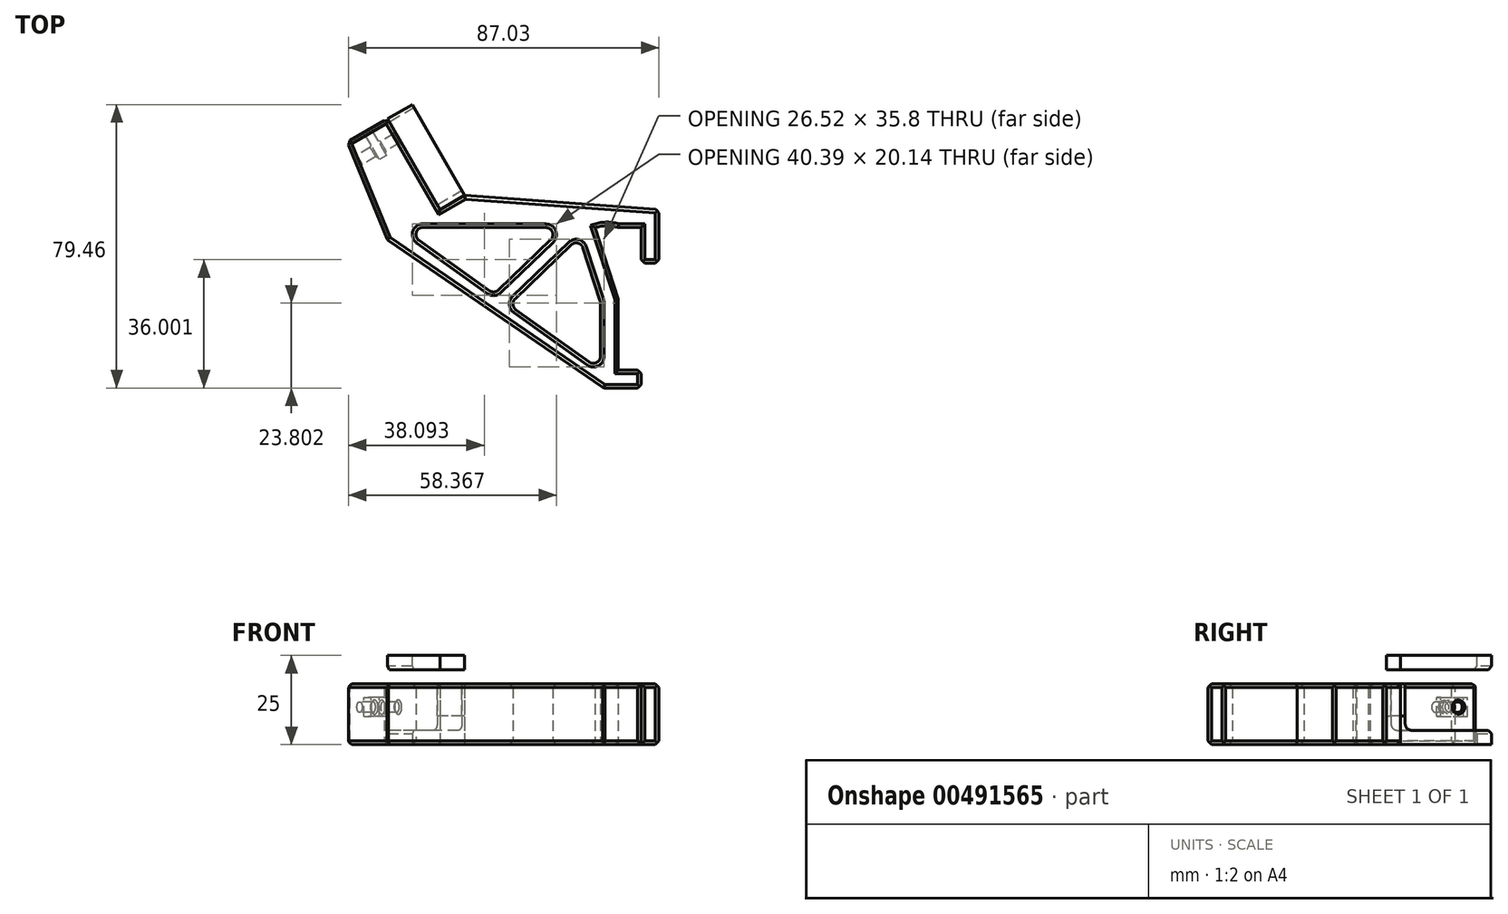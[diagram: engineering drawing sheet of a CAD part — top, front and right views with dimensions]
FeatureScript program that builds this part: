
annotation { "Feature Type Name" : "Feature", "Feature Type Description" : "" }
export const myFeature = defineFeature(function(context is Context, id is Id, definition is map)
    precondition{}
    {
        {
            assignVariable(context, id + "F0", {"name" : "nutDepth", "anyValue" : 2.32});
        }
        {
            assignVariable(context, id + "F1", {"name" : "rightSide", "anyValue" : 1});
        }
        {
            var Q0;
            Q0=qCreatedBy(makeId("Top.planeOp"),FACE);
            var sketch = newSketch(context, id + "F2", { "sketchPlane" : qUnion([Q0])});
            skLineSegment(sketch, "E0", {"start": v(0, 0) * mm, "end": v(0, 20) * mm});
            skLineSegment(sketch, "E1", {"start": v(0, 0) * mm, "end": v(6.4, 0) * mm});
            skLineSegment(sketch, "E2", {"start": v(6.4, 0) * mm, "end": v(6.4, -5) * mm});
            skLineSegment(sketch, "E3", {"start": v(6.4, -5) * mm, "end": v(-5, -5) * mm});
            skLineSegment(sketch, "E4", {"start": v(0, 40) * mm, "end": v(6.4, 40) * mm});
            skLineSegment(sketch, "E5", {"start": v(6.4, 40) * mm, "end": v(6.4, 30) * mm});
            skLineSegment(sketch, "E6", {"start": v(6.4, 30) * mm, "end": v(11.4, 30) * mm});
            skLineSegment(sketch, "E7", {"start": v(11.4, 30) * mm, "end": v(11.4, 45) * mm});
            skLineSegment(sketch, "E8", {"start": v(0, 20) * mm, "end": v(-6.5, 40) * mm});
            skArc(sketch, "E9", {"start": v(0, 40) * mm, "mid": v(-3.25, 40.51) * mm, "end": v(-6.5, 40) * mm});
            skLineSegment(sketch, "E10", {"start": v(11.4, 45) * mm, "end": v(0, 45) * mm, "construction": true});
            skLineSegment(sketch, "E11", {"start": v(0, 45) * mm, "end": v(-50, 45) * mm, "construction": true});
            skLineSegment(sketch, "E12", {"start": v(-50, 45) * mm, "end": v(11.4, 45) * mm, "construction": true});
            skLineSegment(sketch, "E13", {"start": v(-50, 45) * mm, "end": v(-64.7, 70.46) * mm});
            skLineSegment(sketch, "E14", {"start": v(-50, 45) * mm, "end": v(-43.07, 49) * mm});
            skLineSegment(sketch, "E15", {"start": v(-64.7, 70.46) * mm, "end": v(-75.96, 63.96) * mm});
            skLineSegment(sketch, "E16", {"start": v(-50, 45) * mm, "end": v(-54.33, 42.5) * mm, "construction": true});
            skLineSegment(sketch, "E17", {"start": v(-64.7, 70.46) * mm, "end": v(-61.7, 65.26) * mm, "construction": true});
            skLineSegment(sketch, "E18.0", {"start": v(-5, 3.9) * mm, "end": v(-5, 18.9) * mm});
            skLineSegment(sketch, "E19.0", {"start": v(-5.1, 19.5) * mm, "end": v(-9.91, 34.32) * mm});
            skLineSegment(sketch, "E20", {"start": v(-40.93, 40) * mm, "end": v(-20.33, 40) * mm});
            skLineSegment(sketch, "E21", {"start": v(-43.07, 49) * mm, "end": v(11.4, 45) * mm});
            skPoint(sketch, "E22.0.midPoint", {"position": v(-5.37, 18.33) * mm});
            skLineSegment(sketch, "E23", {"start": v(-75.96, 63.96) * mm, "end": v(-64.7, 36.54) * mm});
            skPoint(sketch, "E24.visualSharp", {"position": v(-61.03, 40.13) * mm});
            skPoint(sketch, "E25.newPointB", {"position": v(15.42, -35.63) * mm});
            skPoint(sketch, "E26.visualSharp", {"position": v(-45.4, 40) * mm});
            skArc(sketch, "E27.filletArc", {"start": v(-5, 18.9) * mm, "mid": v(-5.02, 19.2) * mm, "end": v(-5.1, 19.5) * mm});
            skLineSegment(sketch, "E28", {"start": v(-5, -5) * mm, "end": v(-5, 0) * mm, "construction": true});
            skLineSegment(sketch, "E29", {"start": v(-64.7, 36.54) * mm, "end": v(-4.1, -5) * mm});
            skLineSegment(sketch, "E30", {"start": v(-55.9, 36.44) * mm, "end": v(-36.14, 22.3) * mm});
            skLineSegment(sketch, "E31", {"start": v(-40.93, 40) * mm, "end": v(-52.7, 40.06) * mm});
            skPoint(sketch, "E32.trimOffspring.end.orphan", {"position": v(-66.18, 40.13) * mm});
            skPoint(sketch, "E33.visualSharp", {"position": v(-5, 0) * mm});
            skArc(sketch, "E33.filletArc", {"start": v(-8.16, 2.27) * mm, "mid": v(-6.09, 2.11) * mm, "end": v(-5, 3.9) * mm});
            skLineSegment(sketch, "E34.0", {"start": v(-13.2, 35.15) * mm, "end": v(-28.92, 20.04) * mm});
            skLineSegment(sketch, "E35", {"start": v(-18.94, 36.56) * mm, "end": v(-33.59, 22.48) * mm});
            skLineSegment(sketch, "E36.trimOffspring", {"start": v(-28.7, 16.97) * mm, "end": v(-8.16, 2.27) * mm});
            skArc(sketch, "E37.filletArc", {"start": v(-9.91, 34.32) * mm, "mid": v(-11.33, 35.64) * mm, "end": v(-13.2, 35.15) * mm});
            skPoint(sketch, "E38.visualSharp", {"position": v(-30.65, 18.37) * mm});
            skArc(sketch, "E38.filletArc", {"start": v(-28.92, 20.04) * mm, "mid": v(-29.53, 18.45) * mm, "end": v(-28.7, 16.97) * mm});
            skArc(sketch, "E39.filletArc", {"start": v(-18.94, 36.56) * mm, "mid": v(-18.48, 38.75) * mm, "end": v(-20.33, 40) * mm});
            skPoint(sketch, "E40.visualSharp", {"position": v(-34.79, 21.33) * mm});
            skArc(sketch, "E40.filletArc", {"start": v(-36.14, 22.3) * mm, "mid": v(-34.83, 21.93) * mm, "end": v(-33.59, 22.48) * mm});
            skLineSegment(sketch, "E41", {"start": v(-52.7, 40.06) * mm, "end": v(-54.72, 40.07) * mm});
            skArc(sketch, "E42.filletArc", {"start": v(-54.72, 40.07) * mm, "mid": v(-56.64, 38.69) * mm, "end": v(-55.9, 36.44) * mm});
            skLineSegment(sketch, "E43", {"start": v(0, 20) * mm, "end": v(0, 40) * mm, "construction": true});
            skSolve(sketch);
        }
        {
            var Q0;
            Q0=makeQuery(id+"F2.imprint","IMPRINT",FACE,{"disambiguationData":[TD([[makeQuery(id+"F2.imprint","IMPRINT",EDGE,{"derivedFrom":sQuery(id+"F2.wireOp",EDGE,"E0")}),1.0]])]});
            var Q1;
            Q1=makeQuery(id+"F2.imprint","IMPRINT",FACE,{"disambiguationData":[TD([[makeQuery(id+"F2.imprint","IMPRINT",EDGE,{"derivedFrom":sQuery(id+"F2.wireOp",EDGE,"237edecc-037b-4469-a4d6-ffe34dbb8c16.0")}),-1.0]])]});
            var Q2;
            Q2=makeQuery(id+"F2.imprint","IMPRINT",FACE,{"disambiguationData":[TD([[makeQuery(id+"F2.imprint","IMPRINT",EDGE,{"derivedFrom":sQuery(id+"F2.wireOp",EDGE,"E12")}),1.0]])]});
            var Q3;
            {var subQ1=sQuery(id+"F2.wireOp",EDGE,"eAJWAXpk-Rpyz-sTjt-Ieoh-9hGECF5WtqjO");Q3=makeQuery(id+"F2.imprint","IMPRINT",FACE,{"disambiguationData":[TD([[makeQuery(id+"F2.imprint","IMPRINT",EDGE,{"derivedFrom":subQ1}),-1.0]])]});}
            var Q4;
            Q4=sQuery(id+"F2.wireOp",EDGE,"E16");
            extrude(context, id + "F3", {"entities" : qUnion([Q0, Q1, Q2, Q3]), "surfaceEntities" : qUnion([Q4]), "depth" : 17 * mm, "offsetDistance" : 25 * mm});
        }
        {
            var Q0;
            Q0=makeQuery(id+"F3.opExtrude","SWEPT_FACE",FACE,{"disambiguationData":[OSD([sQuery(id+"F2.wireOp",EDGE,"E13")])]});
            var sketch = newSketch(context, id + "F4", { "sketchPlane" : qUnion([Q0])});
            skPoint(sketch, "E44.0", {"position": v(87.37, 0) * mm});
            skLineSegment(sketch, "E45", {"start": v(87.37, 0) * mm, "end": v(87.37, 17) * mm, "construction": true});
            skCircle(sketch, "E46", {"center": v(87.37, 8.5) * mm, "radius": 1.5 * mm});
            skLineSegment(sketch, "E47", {"start": v(87.37, 8.5) * mm, "end": v(65.47, 8.5) * mm, "construction": true});
            skPoint(sketch, "E48.newPointB", {"position": v(63.97, 17) * mm});
            skPoint(sketch, "E49.newPointA", {"position": v(65.47, 0) * mm});
            skPoint(sketch, "E49.newPointB", {"position": v(63.97, 0) * mm});
            skPoint(sketch, "E50.0", {"position": v(93.37, 0) * mm});
            skLineSegment(sketch, "E51", {"start": v(54.97, 17) * mm, "end": v(93.37, 17) * mm});
            skLineSegment(sketch, "E52", {"start": v(54.97, 17) * mm, "end": v(54.97, 13) * mm, "construction": true});
            skLineSegment(sketch, "E53", {"start": v(67.47, 17) * mm, "end": v(54.97, 17) * mm});
            skPoint(sketch, "E54.orphan", {"position": v(54.97, 0) * mm});
            skLineSegment(sketch, "E55", {"start": v(63.97, 17) * mm, "end": v(63.97, 21) * mm});
            skLineSegment(sketch, "E56", {"start": v(93.37, 17) * mm, "end": v(93.37, 21) * mm});
            skLineSegment(sketch, "E57", {"start": v(93.37, 21) * mm, "end": v(63.97, 21) * mm});
            skLineSegment(sketch, "E58", {"start": v(63.97, 17) * mm, "end": v(63.97, 4) * mm});
            skLineSegment(sketch, "E59", {"start": v(63.97, 4) * mm, "end": v(65.47, 4) * mm});
            skLineSegment(sketch, "E60", {"start": v(65.47, 4) * mm, "end": v(65.47, 15) * mm});
            skLineSegment(sketch, "E61", {"start": v(67.47, 17) * mm, "end": v(93.37, 17) * mm});
            skPoint(sketch, "E62.visualSharp", {"position": v(65.47, 17) * mm});
            skArc(sketch, "E62.filletArc", {"start": v(67.47, 17) * mm, "mid": v(66.06, 16.41) * mm, "end": v(65.47, 15) * mm});
            skLineSegment(sketch, "E63", {"start": v(93.37, 0) * mm, "end": v(93.37, -4) * mm});
            skLineSegment(sketch, "E64", {"start": v(63.97, 0) * mm, "end": v(63.97, -4) * mm});
            skLineSegment(sketch, "E65", {"start": v(63.97, -4) * mm, "end": v(93.37, -4) * mm});
            skLineSegment(sketch, "E66", {"start": v(63.97, 0) * mm, "end": v(63.97, 13) * mm});
            skLineSegment(sketch, "E67", {"start": v(63.97, 13) * mm, "end": v(65.47, 13) * mm});
            skLineSegment(sketch, "E68", {"start": v(65.47, 13) * mm, "end": v(65.47, 2) * mm});
            skLineSegment(sketch, "E69", {"start": v(54.97, 0) * mm, "end": v(67.47, 0) * mm});
            skArc(sketch, "E70.filletArc", {"start": v(65.47, 2) * mm, "mid": v(66.06, 0.59) * mm, "end": v(67.47, 0) * mm});
            skLineSegment(sketch, "E71", {"start": v(54.97, 0) * mm, "end": v(93.37, 0) * mm});
            skSolve(sketch);
        }
        {
            var Q0;
            Q0=makeQuery(id+"F3.opExtrude","SWEPT_FACE",FACE,{"disambiguationData":[OSD([sQuery(id+"F2.wireOp",EDGE,"E13")])]});
            cPlane(context, id + "F5", {"entities" : qUnion([Q0]), "cplaneType" : CPlaneType.OFFSET, "offset" : 6.5 * mm, "oppositeDirection" : true, "width" : 150 * mm, "height" : 150 * mm});
        }
        {
            var Q0;
            Q0=qCreatedBy(id+"F5.planeOp",FACE);
            var sketch = newSketch(context, id + "F6", { "sketchPlane" : qUnion([Q0])});
            skPoint(sketch, "E72.0", {"position": v(87.37, 8.5) * mm});
            skLineSegment(sketch, "E73.bottom", {"start": v(90.05, 5.83) * mm, "end": v(84.7, 5.83) * mm});
            skLineSegment(sketch, "E73.top", {"start": v(90.05, 11.18) * mm, "end": v(84.7, 11.18) * mm});
            skLineSegment(sketch, "E73.left", {"start": v(90.05, 5.83) * mm, "end": v(90.05, 11.18) * mm});
            skLineSegment(sketch, "E73.right", {"start": v(84.7, 5.83) * mm, "end": v(84.7, 11.18) * mm});
            skSolve(sketch);
        }
        {
            var Q0;
            Q0=makeQuery(id+"F3.opExtrude","SWEPT_FACE",FACE,{"disambiguationData":[OSD([sQuery(id+"F2.wireOp",EDGE,"E15")])]});
            var sketch = newSketch(context, id + "F7", { "sketchPlane" : qUnion([Q0])});
            skPoint(sketch, "E74.0", {"position": v(27.3, 8.5) * mm});
            skLineSegment(sketch, "E75.bottom", {"start": v(28.46, 5.83) * mm, "end": v(26.14, 5.83) * mm});
            skLineSegment(sketch, "E75.top", {"start": v(28.46, 11.18) * mm, "end": v(26.14, 11.18) * mm});
            skLineSegment(sketch, "E75.left", {"start": v(28.46, 5.83) * mm, "end": v(28.46, 11.18) * mm});
            skLineSegment(sketch, "E75.right", {"start": v(26.14, 5.83) * mm, "end": v(26.14, 11.18) * mm});
            skSolve(sketch);
        }
        {
            var Q0;
            {var subQ1=sQuery(id+"F4.wireOp",EDGE,"E55");Q0=makeQuery(id+"F4.imprint","IMPRINT",FACE,{"disambiguationData":[TD([[makeQuery(id+"F4.imprint","IMPRINT",EDGE,{"derivedFrom":subQ1}),-1.0]])]});}
            var Q1;
            {var subQ1=sQuery(id+"F4.wireOp",EDGE,"E58");Q1=makeQuery(id+"F4.imprint","IMPRINT",FACE,{"disambiguationData":[TD([[makeQuery(id+"F4.imprint","IMPRINT",EDGE,{"derivedFrom":subQ1}),1.0]])]});}
            var Q2;
            {var subQ0=sQuery(id+"F4.wireOp",EDGE,"E59");Q2=makeQuery(id+"F4.imprint","IMPRINT",FACE,{"disambiguationData":[TD([[makeQuery(id+"F4.imprint","IMPRINT",EDGE,{"derivedFrom":subQ0}),1.0]])]});}
            var Q3;
            Q3=makeQuery(id+"F3.opExtrude","CAP_VERTEX",VERTEX,{"disambiguationData":[OSD([sQuery(id+"F2.wireOp",EDGE,"E14"),sQuery(id+"F2.wireOp",EDGE,"E21")])],"isStart":false});
            extrude(context, id + "F8", {"entities" : qUnion([Q0, Q1, Q2]), "endBound" : BoundingType.UP_TO_VERTEX, "depth" : 25 * mm, "endBoundEntityVertex" : qUnion([Q3]), "offsetDistance" : 25 * mm});
        }
        {
            var Q0;
            Q0=makeQuery(id+"F4.imprint","IMPRINT",FACE,{"disambiguationData":[TD([[makeQuery(id+"F4.imprint","IMPRINT",EDGE,{"derivedFrom":sQuery(id+"F4.wireOp",EDGE,"E63")}),-1.0]])]});
            var Q1;
            {var subQ2=sQuery(id+"F4.wireOp",EDGE,"E59");Q1=makeQuery(id+"F4.imprint","IMPRINT",FACE,{"disambiguationData":[TD([[makeQuery(id+"F4.imprint","IMPRINT",EDGE,{"derivedFrom":subQ2}),-1.0]])]});}
            var Q2;
            {var subQ0=sQuery(id+"F4.wireOp",EDGE,"E59");Q2=makeQuery(id+"F4.imprint","IMPRINT",FACE,{"disambiguationData":[TD([[makeQuery(id+"F4.imprint","IMPRINT",EDGE,{"derivedFrom":subQ0}),1.0]])]});}
            var Q3;
            Q3=makeQuery(id+"F3.opExtrude","CAP_VERTEX",VERTEX,{"disambiguationData":[OSD([sQuery(id+"F2.wireOp",EDGE,"E14"),sQuery(id+"F2.wireOp",EDGE,"E21")])],"isStart":true});
            extrude(context, id + "F9", {"entities" : qUnion([Q0, Q1, Q2]), "endBound" : BoundingType.UP_TO_VERTEX, "depth" : 25 * mm, "endBoundEntityVertex" : qUnion([Q3]), "offsetDistance" : 25 * mm});
        }
        {
            var Q0;
            Q0=makeQuery(id+"F3.opExtrude","SWEPT_BODY",BODY,{"disambiguationData":[OSD([sQuery(id+"F2.wireOp",EDGE,"E0"),sQuery(id+"F2.wireOp",EDGE,"E1"),sQuery(id+"F2.wireOp",EDGE,"E2"),sQuery(id+"F2.wireOp",EDGE,"E3"),sQuery(id+"F2.wireOp",EDGE,"E4"),sQuery(id+"F2.wireOp",EDGE,"E5"),sQuery(id+"F2.wireOp",EDGE,"E6"),sQuery(id+"F2.wireOp",EDGE,"E7"),sQuery(id+"F2.wireOp",EDGE,"E8"),sQuery(id+"F2.wireOp",EDGE,"E9"),sQuery(id+"F2.wireOp",EDGE,"E13"),sQuery(id+"F2.wireOp",EDGE,"E14"),sQuery(id+"F2.wireOp",EDGE,"E15"),sQuery(id+"F2.wireOp",EDGE,"7qrmeema-m3dN-8NQb-cVJC-M2zYx1wuRhwV"),sQuery(id+"F2.wireOp",EDGE,"6VCsJ3HK-0u1t-Ih2i-O1FZ-N2a4FtfJKVMv"),sQuery(id+"F2.wireOp",EDGE,"0d49a011-dde0-4b34-802a-ba4be7982d17.0"),sQuery(id+"F2.wireOp",EDGE,"E18.0"),sQuery(id+"F2.wireOp",EDGE,"E19.0"),sQuery(id+"F2.wireOp",EDGE,"L1wIR9CE-IYYx-3uSX-qxFK-d5bkXO2tMUlf"),sQuery(id+"F2.wireOp",EDGE,"E20"),sQuery(id+"F2.wireOp",EDGE,"E21"),sQuery(id+"F2.wireOp",EDGE,"eAJWAXpk-Rpyz-sTjt-Ieoh-9hGECF5WtqjO"),sQuery(id+"F2.wireOp",EDGE,"E23"),sQuery(id+"F2.wireOp",EDGE,"a7916468-2f38-4ad0-9a1b-73fe8f5a6af5.0"),sQuery(id+"F2.wireOp",EDGE,"424dda09-a3cf-40ab-af31-a7be946b1da2.0"),sQuery(id+"F2.wireOp",EDGE,"f569f8be-a630-4df1-b275-36ec8882e1c8.filletArc"),sQuery(id+"F2.wireOp",EDGE,"E24.filletArc"),sQuery(id+"F2.wireOp",EDGE,"E25.filletArc"),sQuery(id+"F2.wireOp",EDGE,"g6ZVx5hb-orSW-Naj4-8hue-9VV4xZY1vNXi"),sQuery(id+"F2.wireOp",EDGE,"E26.filletArc"),sQuery(id+"F2.wireOp",EDGE,"d4f3d028-ac7f-46af-bbb1-e3bfc8b04f52.filletArc"),sQuery(id+"F2.wireOp",EDGE,"9ab228a8-bd1e-4b44-88f1-574d657e2129.filletArc"),sQuery(id+"F2.wireOp",EDGE,"E27.filletArc")])]});
            transform(context, id + "F10", {"entities" : qUnion([Q0]), "transformType" : TransformType.TRANSLATION_3D, "dx" : 0 * mm, "dy" : 0 * mm, "dz" : ((getVariable(context, 'rightSide') == 1) ? -4 : 4) * mm, "makeCopy" : false});
        }
        {
            var Q0;
            Q0=makeQuery(id+"F7.imprint","IMPRINT",FACE,{"disambiguationData":[TD([[makeQuery(id+"F7.imprint","IMPRINT",EDGE,{"derivedFrom":sQuery(id+"F7.wireOp",EDGE,"E75.bottom")}),-1.0]])]});
            extrude(context, id + "F11", {"entities" : qUnion([Q0]), "oppositeDirection" : true, "depth" : 4 * mm, "offsetDistance" : 25 * mm});
        }
        {
            var Q0;
            Q0=makeQuery(id+"F6.imprint","IMPRINT",FACE,{"disambiguationData":[TD([[makeQuery(id+"F6.imprint","IMPRINT",EDGE,{"derivedFrom":sQuery(id+"F6.wireOp",EDGE,"E73.bottom")}),-1.0]])]});
            extrude(context, id + "F12", {"entities" : qUnion([Q0]), "endBound" : BoundingType.SYMMETRIC, "depth" : (getVariable(context, 'nutDepth')) * mm, "offsetDistance" : 25 * mm});
        }
        {
            var Q0;
            Q0=makeQuery(id+"F4.imprint","IMPRINT",FACE,{"disambiguationData":[TD([[makeQuery(id+"F4.imprint","IMPRINT",EDGE,{"derivedFrom":sQuery(id+"F4.wireOp",EDGE,"E46")}),1.0]])]});
            var Q1;
            Q1=sQuery(id+"F4.wireOp",EDGE,"E46");
            extrude(context, id + "F13", {"entities" : qUnion([Q0]), "surfaceEntities" : qUnion([Q1]), "endBound" : BoundingType.SYMMETRIC, "depth" : 25 * mm, "offsetDistance" : 25 * mm});
        }
        {
            var Q0;
            Q0=makeQuery(id+"F11.opExtrude","SWEPT_BODY",BODY,{"disambiguationData":[OSD([sQuery(id+"F7.wireOp",EDGE,"E75.bottom"),sQuery(id+"F7.wireOp",EDGE,"E75.top"),sQuery(id+"F7.wireOp",EDGE,"E75.left"),sQuery(id+"F7.wireOp",EDGE,"E75.right")])]});
            var Q1;
            Q1=makeQuery(id+"F12.opExtrude","SWEPT_BODY",BODY,{"disambiguationData":[OSD([sQuery(id+"F6.wireOp",EDGE,"E73.bottom"),sQuery(id+"F6.wireOp",EDGE,"E73.top"),sQuery(id+"F6.wireOp",EDGE,"E73.left"),sQuery(id+"F6.wireOp",EDGE,"E73.right")])]});
            var Q2;
            Q2=makeQuery(id+"F13.opExtrude","SWEPT_BODY",BODY,{"disambiguationData":[OSD([sQuery(id+"F4.wireOp",EDGE,"E46")])]});
            booleanBodies(context, id + "F14", {"operationType" : BooleanOperationType.UNION, "tools" : qUnion([Q0, Q1, Q2])});
        }
        {
            var Q0;
            Q0=makeQuery(id+"F11.opExtrude","SWEPT_BODY",BODY,{"disambiguationData":[OSD([sQuery(id+"F7.wireOp",EDGE,"E75.bottom"),sQuery(id+"F7.wireOp",EDGE,"E75.top"),sQuery(id+"F7.wireOp",EDGE,"E75.left"),sQuery(id+"F7.wireOp",EDGE,"E75.right")])]});
            transform(context, id + "F15", {"entities" : qUnion([Q0]), "transformType" : TransformType.TRANSLATION_3D, "dx" : 0 * mm, "dy" : 0 * mm, "dz" : ((getVariable(context, 'rightSide') == 1) ? -2 : 2) * mm, "makeCopy" : false});
        }
        {
            var Q0;
            Q0=makeQuery(id+"F11.opExtrude","SWEPT_BODY",BODY,{"disambiguationData":[OSD([sQuery(id+"F7.wireOp",EDGE,"E75.bottom"),sQuery(id+"F7.wireOp",EDGE,"E75.top"),sQuery(id+"F7.wireOp",EDGE,"E75.left"),sQuery(id+"F7.wireOp",EDGE,"E75.right")])]});
            var Q1;
            Q1=makeQuery(id+"F3.opExtrude","SWEPT_BODY",BODY,{"disambiguationData":[OSD([sQuery(id+"F2.wireOp",EDGE,"E0"),sQuery(id+"F2.wireOp",EDGE,"E1"),sQuery(id+"F2.wireOp",EDGE,"E2"),sQuery(id+"F2.wireOp",EDGE,"E3"),sQuery(id+"F2.wireOp",EDGE,"E4"),sQuery(id+"F2.wireOp",EDGE,"E5"),sQuery(id+"F2.wireOp",EDGE,"E6"),sQuery(id+"F2.wireOp",EDGE,"E7"),sQuery(id+"F2.wireOp",EDGE,"E8"),sQuery(id+"F2.wireOp",EDGE,"E9"),sQuery(id+"F2.wireOp",EDGE,"E13"),sQuery(id+"F2.wireOp",EDGE,"E14"),sQuery(id+"F2.wireOp",EDGE,"E15"),sQuery(id+"F2.wireOp",EDGE,"7qrmeema-m3dN-8NQb-cVJC-M2zYx1wuRhwV"),sQuery(id+"F2.wireOp",EDGE,"6VCsJ3HK-0u1t-Ih2i-O1FZ-N2a4FtfJKVMv"),sQuery(id+"F2.wireOp",EDGE,"0d49a011-dde0-4b34-802a-ba4be7982d17.0"),sQuery(id+"F2.wireOp",EDGE,"E18.0"),sQuery(id+"F2.wireOp",EDGE,"E19.0"),sQuery(id+"F2.wireOp",EDGE,"L1wIR9CE-IYYx-3uSX-qxFK-d5bkXO2tMUlf"),sQuery(id+"F2.wireOp",EDGE,"E20"),sQuery(id+"F2.wireOp",EDGE,"E21"),sQuery(id+"F2.wireOp",EDGE,"eAJWAXpk-Rpyz-sTjt-Ieoh-9hGECF5WtqjO"),sQuery(id+"F2.wireOp",EDGE,"E23"),sQuery(id+"F2.wireOp",EDGE,"a7916468-2f38-4ad0-9a1b-73fe8f5a6af5.0"),sQuery(id+"F2.wireOp",EDGE,"424dda09-a3cf-40ab-af31-a7be946b1da2.0"),sQuery(id+"F2.wireOp",EDGE,"f569f8be-a630-4df1-b275-36ec8882e1c8.filletArc"),sQuery(id+"F2.wireOp",EDGE,"E24.filletArc"),sQuery(id+"F2.wireOp",EDGE,"E25.filletArc"),sQuery(id+"F2.wireOp",EDGE,"g6ZVx5hb-orSW-Naj4-8hue-9VV4xZY1vNXi"),sQuery(id+"F2.wireOp",EDGE,"E26.filletArc"),sQuery(id+"F2.wireOp",EDGE,"d4f3d028-ac7f-46af-bbb1-e3bfc8b04f52.filletArc"),sQuery(id+"F2.wireOp",EDGE,"9ab228a8-bd1e-4b44-88f1-574d657e2129.filletArc"),sQuery(id+"F2.wireOp",EDGE,"E27.filletArc")])]});
            booleanBodies(context, id + "F16", {"operationType" : BooleanOperationType.SUBTRACTION, "tools" : qUnion([Q0]), "targets" : qUnion([Q1])});
        }
        {
            var Q0;
            Q0=makeQuery(id+"F3.opExtrude","CAP_FACE",FACE,{"disambiguationData":[OSD([sQuery(id+"F2.wireOp",EDGE,"E0"),sQuery(id+"F2.wireOp",EDGE,"E1"),sQuery(id+"F2.wireOp",EDGE,"E2"),sQuery(id+"F2.wireOp",EDGE,"E3"),sQuery(id+"F2.wireOp",EDGE,"E4"),sQuery(id+"F2.wireOp",EDGE,"E5"),sQuery(id+"F2.wireOp",EDGE,"E6"),sQuery(id+"F2.wireOp",EDGE,"E7"),sQuery(id+"F2.wireOp",EDGE,"E8"),sQuery(id+"F2.wireOp",EDGE,"E9"),sQuery(id+"F2.wireOp",EDGE,"E13"),sQuery(id+"F2.wireOp",EDGE,"E14"),sQuery(id+"F2.wireOp",EDGE,"E15"),sQuery(id+"F2.wireOp",EDGE,"7qrmeema-m3dN-8NQb-cVJC-M2zYx1wuRhwV"),sQuery(id+"F2.wireOp",EDGE,"6VCsJ3HK-0u1t-Ih2i-O1FZ-N2a4FtfJKVMv"),sQuery(id+"F2.wireOp",EDGE,"E21"),sQuery(id+"F2.wireOp",EDGE,"E22.0"),sQuery(id+"F2.wireOp",EDGE,"E22.1"),sQuery(id+"F2.wireOp",EDGE,"E22.2"),sQuery(id+"F2.wireOp",EDGE,"E22.3"),sQuery(id+"F2.wireOp",EDGE,"E22.4"),sQuery(id+"F2.wireOp",EDGE,"E22.5"),sQuery(id+"F2.wireOp",EDGE,"b3c4abfa-e79e-4871-9c84-433da5bf6959.0"),sQuery(id+"F2.wireOp",EDGE,"b3c4abfa-e79e-4871-9c84-433da5bf6959.1"),sQuery(id+"F2.wireOp",EDGE,"b3c4abfa-e79e-4871-9c84-433da5bf6959.2"),sQuery(id+"F2.wireOp",EDGE,"b3c4abfa-e79e-4871-9c84-433da5bf6959.3"),sQuery(id+"F2.wireOp",EDGE,"b3c4abfa-e79e-4871-9c84-433da5bf6959.4"),sQuery(id+"F2.wireOp",EDGE,"b3c4abfa-e79e-4871-9c84-433da5bf6959.5"),sQuery(id+"F2.wireOp",EDGE,"5098edf1-84d6-4787-bb65-a0afb68e6647.0"),sQuery(id+"F2.wireOp",EDGE,"5098edf1-84d6-4787-bb65-a0afb68e6647.1"),sQuery(id+"F2.wireOp",EDGE,"5098edf1-84d6-4787-bb65-a0afb68e6647.2"),sQuery(id+"F2.wireOp",EDGE,"5098edf1-84d6-4787-bb65-a0afb68e6647.3"),sQuery(id+"F2.wireOp",EDGE,"5098edf1-84d6-4787-bb65-a0afb68e6647.4"),sQuery(id+"F2.wireOp",EDGE,"5098edf1-84d6-4787-bb65-a0afb68e6647.5"),sQuery(id+"F2.wireOp",EDGE,"eAJWAXpk-Rpyz-sTjt-Ieoh-9hGECF5WtqjO"),sQuery(id+"F2.wireOp",EDGE,"E23"),sQuery(id+"F2.wireOp",EDGE,"a7916468-2f38-4ad0-9a1b-73fe8f5a6af5.0"),sQuery(id+"F2.wireOp",EDGE,"424dda09-a3cf-40ab-af31-a7be946b1da2.0"),sQuery(id+"F2.wireOp",EDGE,"f569f8be-a630-4df1-b275-36ec8882e1c8.filletArc"),sQuery(id+"F2.wireOp",EDGE,"E24.filletArc"),sQuery(id+"F2.wireOp",EDGE,"E25.filletArc"),sQuery(id+"F2.wireOp",EDGE,"g6ZVx5hb-orSW-Naj4-8hue-9VV4xZY1vNXi")])],"isStart":false});
            var Q1;
            Q1=makeQuery(id+"F3.opExtrude","CAP_FACE",FACE,{"disambiguationData":[OSD([sQuery(id+"F2.wireOp",EDGE,"E0"),sQuery(id+"F2.wireOp",EDGE,"E1"),sQuery(id+"F2.wireOp",EDGE,"E2"),sQuery(id+"F2.wireOp",EDGE,"E3"),sQuery(id+"F2.wireOp",EDGE,"E4"),sQuery(id+"F2.wireOp",EDGE,"E5"),sQuery(id+"F2.wireOp",EDGE,"E6"),sQuery(id+"F2.wireOp",EDGE,"E7"),sQuery(id+"F2.wireOp",EDGE,"E8"),sQuery(id+"F2.wireOp",EDGE,"E9"),sQuery(id+"F2.wireOp",EDGE,"E13"),sQuery(id+"F2.wireOp",EDGE,"E14"),sQuery(id+"F2.wireOp",EDGE,"E15"),sQuery(id+"F2.wireOp",EDGE,"7qrmeema-m3dN-8NQb-cVJC-M2zYx1wuRhwV"),sQuery(id+"F2.wireOp",EDGE,"6VCsJ3HK-0u1t-Ih2i-O1FZ-N2a4FtfJKVMv"),sQuery(id+"F2.wireOp",EDGE,"E21"),sQuery(id+"F2.wireOp",EDGE,"E22.0"),sQuery(id+"F2.wireOp",EDGE,"E22.1"),sQuery(id+"F2.wireOp",EDGE,"E22.2"),sQuery(id+"F2.wireOp",EDGE,"E22.3"),sQuery(id+"F2.wireOp",EDGE,"E22.4"),sQuery(id+"F2.wireOp",EDGE,"E22.5"),sQuery(id+"F2.wireOp",EDGE,"b3c4abfa-e79e-4871-9c84-433da5bf6959.0"),sQuery(id+"F2.wireOp",EDGE,"b3c4abfa-e79e-4871-9c84-433da5bf6959.1"),sQuery(id+"F2.wireOp",EDGE,"b3c4abfa-e79e-4871-9c84-433da5bf6959.2"),sQuery(id+"F2.wireOp",EDGE,"b3c4abfa-e79e-4871-9c84-433da5bf6959.3"),sQuery(id+"F2.wireOp",EDGE,"b3c4abfa-e79e-4871-9c84-433da5bf6959.4"),sQuery(id+"F2.wireOp",EDGE,"b3c4abfa-e79e-4871-9c84-433da5bf6959.5"),sQuery(id+"F2.wireOp",EDGE,"5098edf1-84d6-4787-bb65-a0afb68e6647.0"),sQuery(id+"F2.wireOp",EDGE,"5098edf1-84d6-4787-bb65-a0afb68e6647.1"),sQuery(id+"F2.wireOp",EDGE,"5098edf1-84d6-4787-bb65-a0afb68e6647.2"),sQuery(id+"F2.wireOp",EDGE,"5098edf1-84d6-4787-bb65-a0afb68e6647.3"),sQuery(id+"F2.wireOp",EDGE,"5098edf1-84d6-4787-bb65-a0afb68e6647.4"),sQuery(id+"F2.wireOp",EDGE,"5098edf1-84d6-4787-bb65-a0afb68e6647.5"),sQuery(id+"F2.wireOp",EDGE,"eAJWAXpk-Rpyz-sTjt-Ieoh-9hGECF5WtqjO"),sQuery(id+"F2.wireOp",EDGE,"E23"),sQuery(id+"F2.wireOp",EDGE,"a7916468-2f38-4ad0-9a1b-73fe8f5a6af5.0"),sQuery(id+"F2.wireOp",EDGE,"424dda09-a3cf-40ab-af31-a7be946b1da2.0"),sQuery(id+"F2.wireOp",EDGE,"f569f8be-a630-4df1-b275-36ec8882e1c8.filletArc"),sQuery(id+"F2.wireOp",EDGE,"E24.filletArc"),sQuery(id+"F2.wireOp",EDGE,"E25.filletArc"),sQuery(id+"F2.wireOp",EDGE,"g6ZVx5hb-orSW-Naj4-8hue-9VV4xZY1vNXi")])],"isStart":true});
            chamfer(context, id + "F17", {"entities" : qUnion([Q0, Q1]), "width" : 1 * mm, "tangentPropagation" : true});
        }
        {
            var Q0;
            {var subQ0=sQuery(id+"F4.wireOp",EDGE,"E46");Q0=makeQuery(id+"F16.opBoolean","INTERSECT",EDGE,{"derivedFrom":[makeQuery(id+"F3.opExtrude","SWEPT_FACE",FACE,{"disambiguationData":[OSD([sQuery(id+"F2.wireOp",EDGE,"E13")])]}),makeQuery(id+"F14.opBoolean","SPLIT",FACE,{"disambiguationData":[TD([makeQuery(id+"F11.opExtrude","SWEPT_FACE",FACE,{"disambiguationData":[OSD([sQuery(id+"F7.wireOp",EDGE,"E75.right")])]})])],"derivedFrom":makeQuery(id+"F13.opExtrude","SWEPT_FACE",FACE,{"disambiguationData":[OSD([subQ0])]})})]});}
            var Q1;
            {var subQ0=sQuery(id+"F4.wireOp",EDGE,"E46");Q1=makeQuery(id+"F16.opBoolean","INTERSECT",EDGE,{"derivedFrom":[makeQuery(id+"F3.opExtrude","SWEPT_FACE",FACE,{"disambiguationData":[OSD([sQuery(id+"F2.wireOp",EDGE,"E23")])]}),makeQuery(id+"F14.opBoolean","SPLIT",FACE,{"disambiguationData":[TD([makeQuery(id+"F11.opExtrude","SWEPT_FACE",FACE,{"disambiguationData":[OSD([sQuery(id+"F7.wireOp",EDGE,"E75.left")])]})])],"derivedFrom":makeQuery(id+"F13.opExtrude","SWEPT_FACE",FACE,{"disambiguationData":[OSD([subQ0])]})})]});}
            var Q2;
            Q2=makeQuery(id+"F16.opBoolean","COPY",EDGE,{"derivedFrom":makeQuery(id+"F14.opBoolean","INTERSECT",EDGE,{"derivedFrom":[makeQuery(id+"F12.opExtrude","CAP_FACE",FACE,{"disambiguationData":[OSD([sQuery(id+"F6.wireOp",EDGE,"E73.bottom"),sQuery(id+"F6.wireOp",EDGE,"E73.top"),sQuery(id+"F6.wireOp",EDGE,"E73.left"),sQuery(id+"F6.wireOp",EDGE,"E73.right")])],"isStart":true}),makeQuery(id+"F13.opExtrude","SWEPT_FACE",FACE,{"disambiguationData":[OSD([sQuery(id+"F4.wireOp",EDGE,"E46")])]})]})});
            var Q3;
            Q3=makeQuery(id+"F16.opBoolean","COPY",EDGE,{"derivedFrom":makeQuery(id+"F14.opBoolean","INTERSECT",EDGE,{"derivedFrom":[makeQuery(id+"F12.opExtrude","CAP_FACE",FACE,{"disambiguationData":[OSD([sQuery(id+"F6.wireOp",EDGE,"E73.bottom"),sQuery(id+"F6.wireOp",EDGE,"E73.top"),sQuery(id+"F6.wireOp",EDGE,"E73.left"),sQuery(id+"F6.wireOp",EDGE,"E73.right")])],"isStart":false}),makeQuery(id+"F13.opExtrude","SWEPT_FACE",FACE,{"disambiguationData":[OSD([sQuery(id+"F4.wireOp",EDGE,"E46")])]})]})});
            var Q4;
            Q4=makeQuery(id+"F16.opBoolean","COPY",EDGE,{"derivedFrom":makeQuery(id+"F11.opExtrude","CAP_EDGE",EDGE,{"disambiguationData":[OSD([sQuery(id+"F7.wireOp",EDGE,"E75.right")])],"isStart":true})});
            var Q5;
            Q5=makeQuery(id+"F16.opBoolean","COPY",EDGE,{"derivedFrom":makeQuery(id+"F11.opExtrude","CAP_EDGE",EDGE,{"disambiguationData":[OSD([sQuery(id+"F7.wireOp",EDGE,"E75.left")])],"isStart":true})});
            var Q6;
            Q6=makeQuery(id+"F16.opBoolean","COPY",EDGE,{"derivedFrom":makeQuery(id+"F11.opExtrude","CAP_EDGE",EDGE,{"disambiguationData":[OSD([sQuery(id+"F7.wireOp",EDGE,"E75.bottom")])],"isStart":true})});
            var Q7;
            Q7=makeQuery(id+"F16.opBoolean","COPY",EDGE,{"derivedFrom":makeQuery(id+"F11.opExtrude","CAP_EDGE",EDGE,{"disambiguationData":[OSD([sQuery(id+"F7.wireOp",EDGE,"E75.top")])],"isStart":true})});
            chamfer(context, id + "F18", {"entities" : qUnion([Q0, Q1, Q2, Q3, Q4, Q5, Q6, Q7]), "width" : 0.5 * mm, "tangentPropagation" : true});
        }
        {
            var Q0;
            Q0=makeQuery(id+"F3.opExtrude","SWEPT_EDGE",EDGE,{"disambiguationData":[OSD([sQuery(id+"F2.wireOp",EDGE,"E5"),sQuery(id+"F2.wireOp",EDGE,"E6")])]});
            var Q1;
            Q1=makeQuery(id+"F3.opExtrude","SWEPT_EDGE",EDGE,{"disambiguationData":[OSD([sQuery(id+"F2.wireOp",EDGE,"E6"),sQuery(id+"F2.wireOp",EDGE,"E7")])]});
            var Q2;
            Q2=makeQuery(id+"F3.opExtrude","SWEPT_EDGE",EDGE,{"disambiguationData":[OSD([sQuery(id+"F2.wireOp",EDGE,"E7"),sQuery(id+"F2.wireOp",EDGE,"E21")])]});
            var Q3;
            Q3=makeQuery(id+"F3.opExtrude","SWEPT_EDGE",EDGE,{"disambiguationData":[OSD([sQuery(id+"F2.wireOp",EDGE,"E2"),sQuery(id+"F2.wireOp",EDGE,"E3")])]});
            var Q4;
            Q4=makeQuery(id+"F3.opExtrude","SWEPT_EDGE",EDGE,{"disambiguationData":[OSD([sQuery(id+"F2.wireOp",EDGE,"E1"),sQuery(id+"F2.wireOp",EDGE,"E2")])]});
            var Q5;
            Q5=makeQuery(id+"F3.opExtrude","SWEPT_EDGE",EDGE,{"disambiguationData":[OSD([sQuery(id+"F2.wireOp",EDGE,"E3"),sQuery(id+"F2.wireOp",EDGE,"g6ZVx5hb-orSW-Naj4-8hue-9VV4xZY1vNXi")])]});
            var Q6;
            Q6=makeQuery(id+"F3.opExtrude","SWEPT_EDGE",EDGE,{"disambiguationData":[OSD([sQuery(id+"F2.wireOp",EDGE,"eAJWAXpk-Rpyz-sTjt-Ieoh-9hGECF5WtqjO"),sQuery(id+"F2.wireOp",EDGE,"E23")])]});
            var Q7;
            Q7=makeQuery(id+"F3.opExtrude","SWEPT_EDGE",EDGE,{"disambiguationData":[OSD([sQuery(id+"F2.wireOp",EDGE,"eAJWAXpk-Rpyz-sTjt-Ieoh-9hGECF5WtqjO"),sQuery(id+"F2.wireOp",EDGE,"g6ZVx5hb-orSW-Naj4-8hue-9VV4xZY1vNXi")])]});
            var Q8;
            Q8=makeQuery(id+"F3.opExtrude","SWEPT_EDGE",EDGE,{"disambiguationData":[OSD([sQuery(id+"F2.wireOp",EDGE,"E15"),sQuery(id+"F2.wireOp",EDGE,"E23")])]});
            var Q9;
            Q9=makeQuery(id+"F3.opExtrude","SWEPT_EDGE",EDGE,{"disambiguationData":[OSD([sQuery(id+"F2.wireOp",EDGE,"E13"),sQuery(id+"F2.wireOp",EDGE,"E15")])]});
            var Q10;
            Q10=makeQuery(id+"F9.opExtrude","SWEPT_EDGE",EDGE,{"disambiguationData":[OSD([sQuery(id+"F2.wireOp",EDGE,"E13"),sQuery(id+"F2.wireOp",EDGE,"E15"),sQuery(id+"F4.wireOp",EDGE,"E63"),sQuery(id+"F4.wireOp",EDGE,"E71")])]});
            var Q11;
            Q11=makeQuery(id+"F9.opExtrude","TWEAK_EDGE",EDGE,{"derivedFrom":[makeQuery(id+"F4.imprint","IMPRINT",EDGE,{"derivedFrom":sQuery(id+"F4.wireOp",EDGE,"E71")}),dummyQuery(id+"F9.vertexPlane.planeOp",FACE)]});
            var Q12;
            Q12=makeQuery(id+"F8.opExtrude","TWEAK_EDGE",EDGE,{"derivedFrom":[makeQuery(id+"F4.imprint","IMPRINT",EDGE,{"derivedFrom":sQuery(id+"F4.wireOp",EDGE,"E61")}),dummyQuery(id+"F8.vertexPlane.planeOp",FACE)]});
            var Q13;
            Q13=makeQuery(id+"F8.opExtrude","SWEPT_EDGE",EDGE,{"disambiguationData":[OSD([sQuery(id+"F2.wireOp",EDGE,"E13"),sQuery(id+"F2.wireOp",EDGE,"E15"),sQuery(id+"F4.wireOp",EDGE,"E56"),sQuery(id+"F4.wireOp",EDGE,"E61")])]});
            chamfer(context, id + "F19", {"entities" : qUnion([Q0, Q1, Q2, Q3, Q4, Q5, Q6, Q7, Q8, Q9, Q10, Q11, Q12, Q13]), "width" : 1 * mm, "tangentPropagation" : true});
        }
    });
